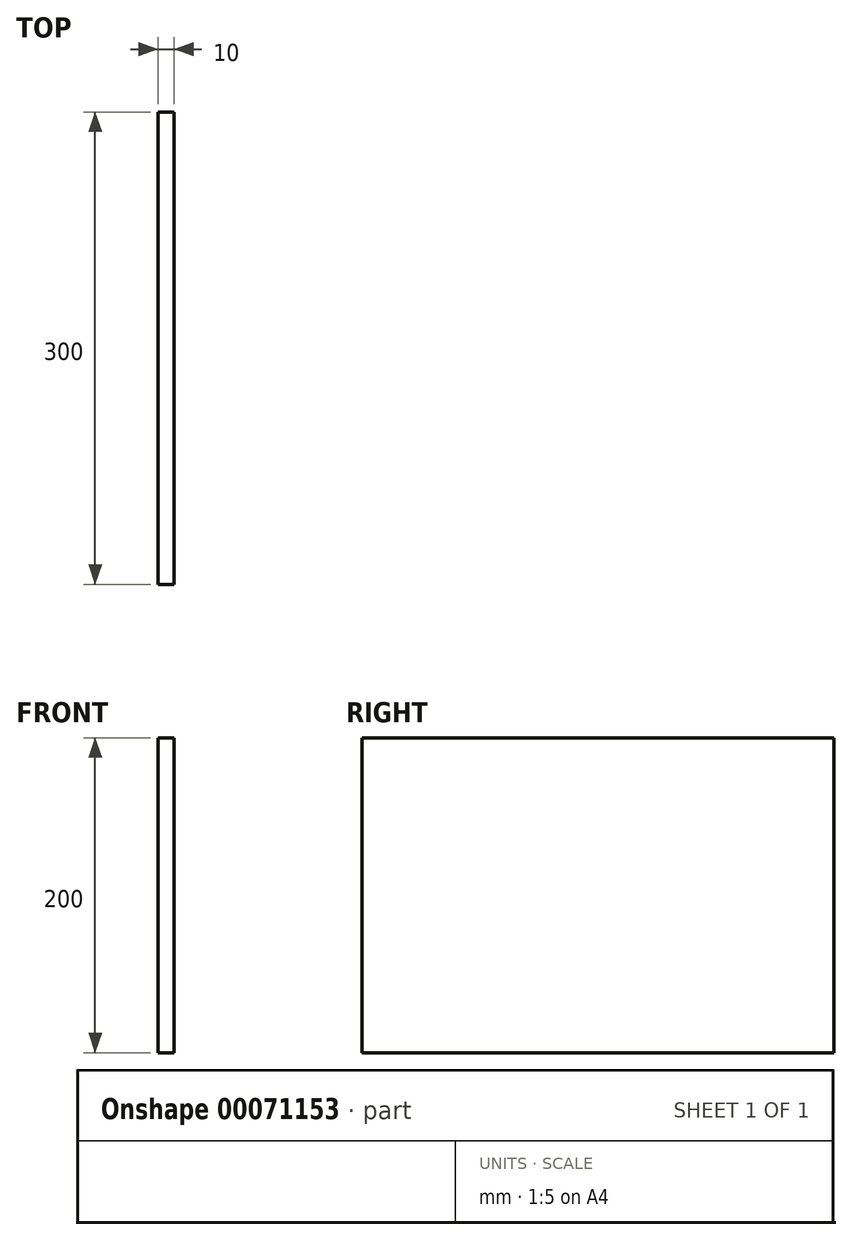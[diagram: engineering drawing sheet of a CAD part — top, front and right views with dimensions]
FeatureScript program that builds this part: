
annotation { "Feature Type Name" : "Feature", "Feature Type Description" : "" }
export const myFeature = defineFeature(function(context is Context, id is Id, definition is map)
    precondition{}
    {
        {
            var Q0;
            Q0=qCreatedBy(makeId("Right.planeOp"),FACE);
            var sketch = newSketch(context, id + "F0", { "sketchPlane" : qUnion([Q0])});
            skLineSegment(sketch, "E0.rect.bottom", {"start": v(-150, 100) * mm, "end": v(150, 100) * mm});
            skLineSegment(sketch, "E0.rect.top", {"start": v(-150, -100) * mm, "end": v(150, -100) * mm});
            skLineSegment(sketch, "E0.rect.left", {"start": v(-150, 100) * mm, "end": v(-150, -100) * mm});
            skLineSegment(sketch, "E0.rect.right", {"start": v(150, 100) * mm, "end": v(150, -100) * mm});
            skPoint(sketch, "E0.rect.middle", {"position": v(0, 0) * mm});
            skSolve(sketch);
        }
        {
            var Q0;
            Q0 = qSketchRegion(id + "F0", true);
            extrude(context, id + "F1", {"entities" : qUnion([Q0]), "depth" : 10 * mm});
        }
    });
